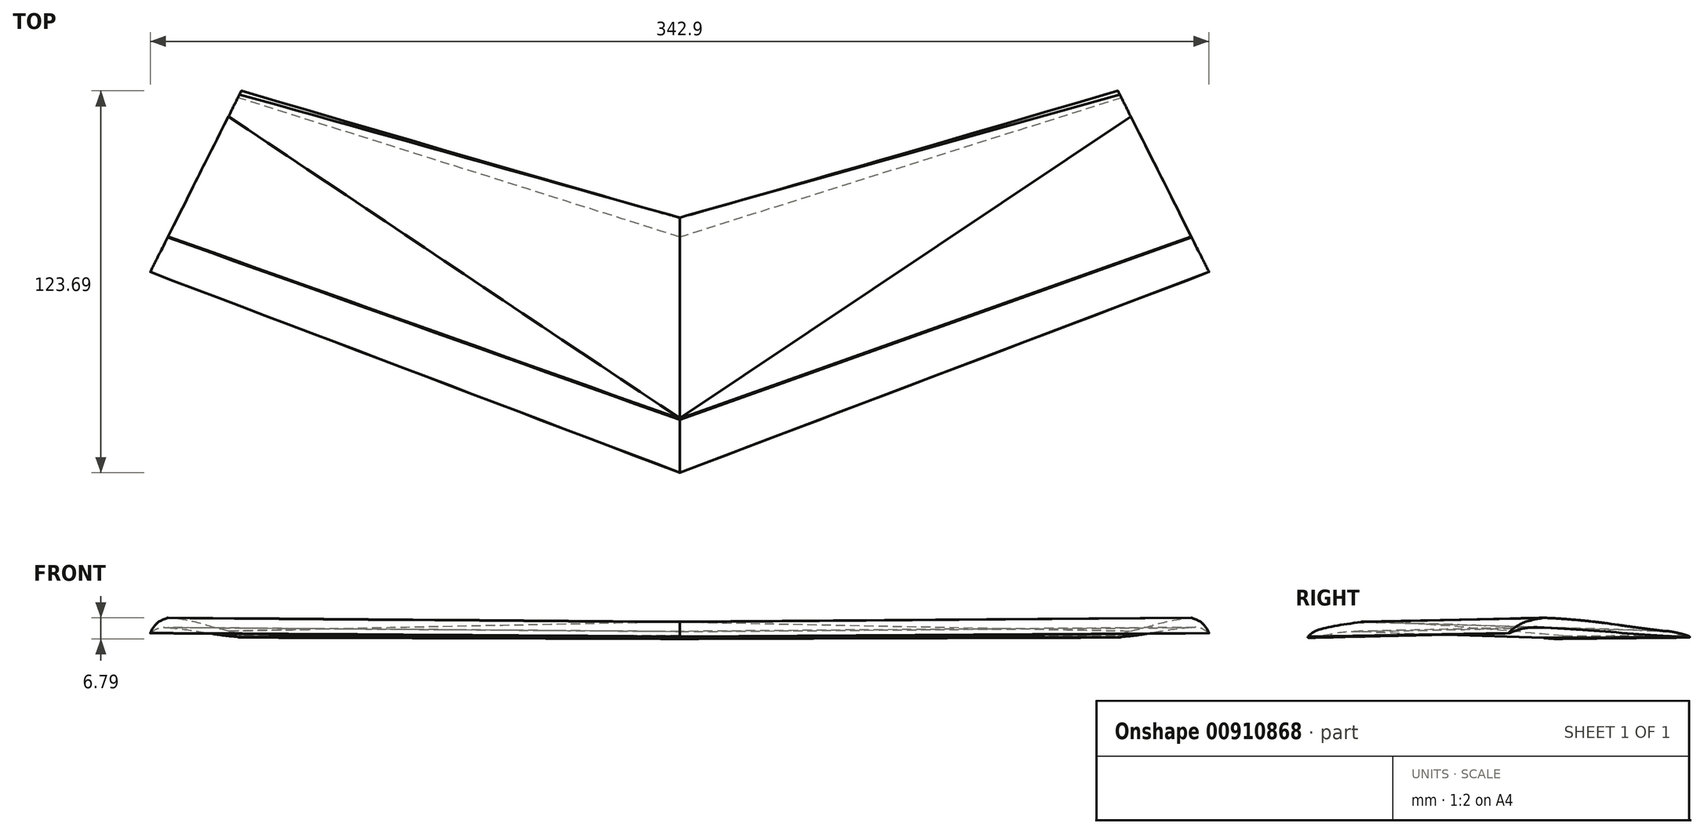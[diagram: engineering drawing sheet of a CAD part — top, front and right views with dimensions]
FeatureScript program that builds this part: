
annotation { "Feature Type Name" : "Feature", "Feature Type Description" : "" }
export const myFeature = defineFeature(function(context is Context, id is Id, definition is map)
    precondition{}
    {
        {
            var Q0;
            Q0=qCreatedBy(makeId("Right.planeOp"),FACE);
            var sketch = newSketch(context, id + "F0", { "sketchPlane" : qUnion([Q0])});
            skArc(sketch, "E0", {"start": v(-0.23, -1.57) * mm, "mid": v(-0.11, -1.58) * mm, "end": v(0, -1.59) * mm});
            skFitSpline(sketch, "E1", {"points": [v(-17.46, -3.17) * mm, v(-15.06, -1.37) * mm, v(-0.36, 1.55) * mm], "startDerivative": vector(5.68, 6.08) * mm, "endDerivative": vector(25.94, 3.66) * mm});
            skFitSpline(sketch, "E2", {"points": [v(65.09, -2.95) * mm, v(22.47, 0.6) * mm, v(0, 1.59) * mm], "startDerivative": vector(-79.34, 7.2) * mm, "endDerivative": vector(-49.23, 1.58) * mm});
            skFitSpline(sketch, "E3", {"points": [v(-17.46, -3.17) * mm, v(-17.46, -3.5) * mm, v(-8, -1.94) * mm, v(-0.23, -1.57) * mm], "startDerivative": vector(-1.8, -4.44) * mm, "endDerivative": vector(15.35, -0.57) * mm});
            skFitSpline(sketch, "E4", {"points": [v(0, -1.59) * mm, v(58.83, -3.63) * mm], "startDerivative": vector(58.83, -2.04) * mm, "endDerivative": vector(58.83, -2.04) * mm});
            skFitSpline(sketch, "E5", {"points": [v(58.83, -3.63) * mm, v(64.82, -3.63) * mm, v(65.09, -2.95) * mm], "startDerivative": vector(10.7, -0.97) * mm, "endDerivative": vector(0.12, 2.96) * mm});
            skArc(sketch, "E6.trimOffspring", {"start": v(0.1, 1.58) * mm, "mid": v(-0.13, 1.58) * mm, "end": v(-0.36, 1.55) * mm});
            skSolve(sketch);
        }
        {
            var Q0;
            Q0=qCreatedBy(makeId("Top.planeOp"),FACE);
            var sketch = newSketch(context, id + "F1", { "sketchPlane" : qUnion([Q0])});
            skLineSegment(sketch, "E7", {"start": v(0, -7.36) * mm, "end": v(158.85, 72.52) * mm});
            skSolve(sketch);
        }
        {
            var Q0;
            Q0=sQuery(id+"F1.wireOp",VERTEX,"E7.end");
            var Q1;
            Q1=sQuery(id+"F1.wireOp",EDGE,"E7");
            cPlane(context, id + "F2", {"entities" : qUnion([Q0, Q1]), "cplaneType" : CPlaneType.LINE_POINT, "offset" : 25.4 * mm, "width" : 152.4 * mm, "height" : 152.4 * mm});
        }
        {
            var Q0;
            Q0=qCreatedBy(id+"F2.planeOp",FACE);
            var sketch = newSketch(context, id + "F3", { "sketchPlane" : qUnion([Q0])});
            skArc(sketch, "E8", {"start": v(-21.9, -0.27) * mm, "mid": v(-21.82, -0.28) * mm, "end": v(-21.75, -0.28) * mm});
            skFitSpline(sketch, "E9", {"points": [v(-34.61, -2.01) * mm, v(-31.24, 0.42) * mm, v(-22.04, 2.85) * mm], "startDerivative": vector(5.68, 6.08) * mm, "endDerivative": vector(25.94, 3.66) * mm});
            skFitSpline(sketch, "E10", {"points": [v(21.78, -1.4) * mm, v(0.72, 1.16) * mm, v(-21.75, 2.89) * mm], "startDerivative": vector(-79.17, 8.68) * mm, "endDerivative": vector(-49.23, 1.58) * mm});
            skFitSpline(sketch, "E11", {"points": [v(-34.61, -2.01) * mm, v(-34.61, -2.1) * mm, v(-29.69, -0.64) * mm, v(-21.9, -0.27) * mm], "startDerivative": vector(-1.13, -4.57) * mm, "endDerivative": vector(15.35, -0.57) * mm});
            skFitSpline(sketch, "E12", {"points": [v(-21.75, -0.28) * mm, v(28.6, -3.25) * mm], "startDerivative": vector(58.83, -2.04) * mm, "endDerivative": vector(58.83, -2.04) * mm});
            skFitSpline(sketch, "E13", {"points": [v(28.6, -3.25) * mm, v(31.07, -3.25) * mm, v(21.78, -1.4) * mm], "startDerivative": vector(11, -2.7) * mm, "endDerivative": vector(-8.76, -0.78) * mm});
            skArc(sketch, "E14.trimOffspring", {"start": v(-21.75, 2.89) * mm, "mid": v(-21.9, 2.88) * mm, "end": v(-22.04, 2.85) * mm});
            skSolve(sketch);
        }
        {
            var Q0;
            Q0 = qSketchRegion(id + "F0", true);
            var Q1;
            Q1 = qSketchRegion(id + "F3", true);
            loft(context, id + "F4", {"sheetProfilesArray" : [{ "sheetProfileEntities" : qUnion([Q0]) }, { "sheetProfileEntities" : qUnion([Q1]) }]});
        }
        {
            var Q0;
            Q0=makeQuery(id+"F4.opLoft","SWEPT_BODY",BODY,{"disambiguationData":[OSD([makeQuery(id+"F0.imprint","IMPRINT",FACE,{"disambiguationData":[TD([[makeQuery(id+"F0.imprint","IMPRINT",EDGE,{"derivedFrom":sQuery(id+"F0.wireOp",EDGE,"E0")}),1.0]])]}),makeQuery(id+"F3.imprint","IMPRINT",FACE,{"disambiguationData":[TD([[makeQuery(id+"F3.imprint","IMPRINT",EDGE,{"derivedFrom":sQuery(id+"F3.wireOp",EDGE,"E8")}),1.0]])]})])]});
            var Q1;
            Q1=qCreatedBy(makeId("Right.planeOp"),FACE);
            mirror(context, id + "F5", {"operationType" : NewBodyOperationType.ADD, "entities" : qUnion([Q0]), "mirrorPlane" : qUnion([Q1])});
        }
    });
